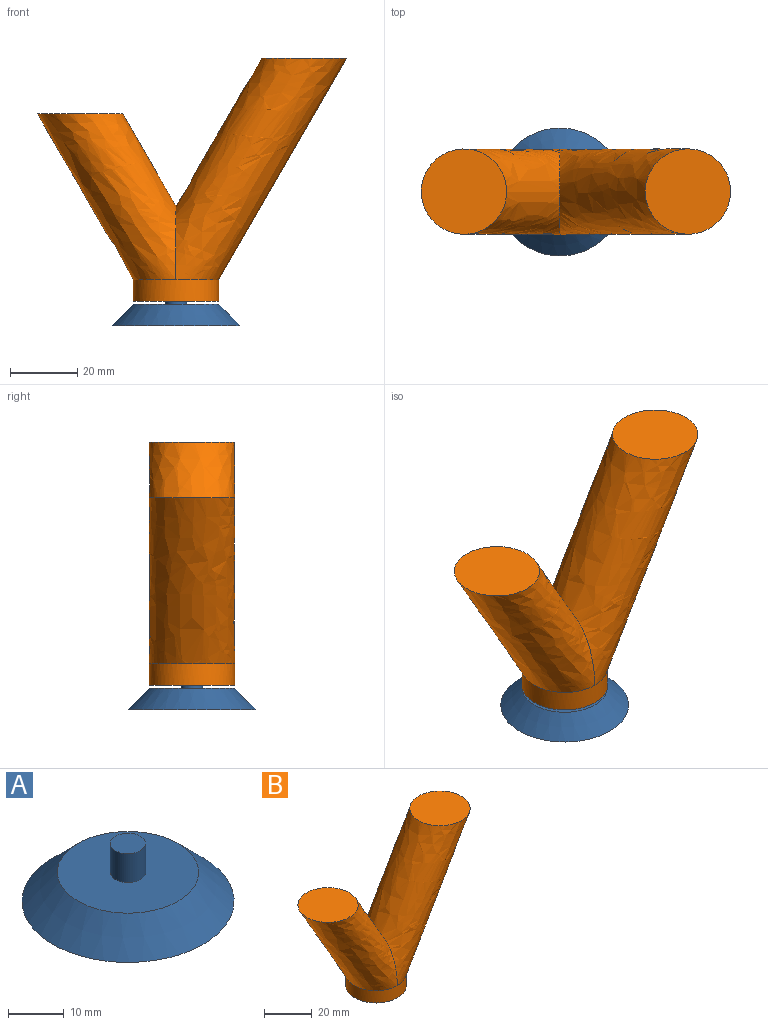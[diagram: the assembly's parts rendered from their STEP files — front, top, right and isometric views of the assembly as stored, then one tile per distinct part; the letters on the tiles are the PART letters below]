
ASSEMBLY  parts=2 mates=1
PART A: 5 faces, bbox 38.1x38.1x12.7 mm
  f0: plane 25.4x25.4mm, normal (0,0,1), area 475mm2, adj f2,f3
  f1: plane 38.1x38.1mm, normal (0,0,-1), area 1140.1mm2, adj f2
  f2: cone r=12.7mm half-angle=45deg, axis (0,0,-1), area 895.7mm2, adj f0,f1
  f3: cylinder r=3.17mm len=6.35mm, axis (0,0,-1), area 126.7mm2, adj f0,f4
  f4: plane 6.35x6.35mm, normal (0,0,1), area 31.7mm2, adj f3
PART B: 8 faces, bbox 95.6x54.3x75.9 mm
  f0: plane 28.93x28.93mm, normal (0,0,1), area 506.7mm2, adj f1
  f1: bspline ~65.99x63.5mm, area 5261.1mm2, adj f0,f3,f4
  f2: plane 28.93x28.93mm, normal (0,0,1), area 506.7mm2, adj f3
  f3: bspline ~53.98x50.8mm, area 3834.1mm2, adj f1,f2,f4
  f4: cylinder r=12.7mm len=25.4mm, axis (0,0,1), area 506.7mm2, adj f1,f3,f5
  f5: plane 25.4x25.4mm, normal (0,0,-1), area 475mm2, adj f4,f6
  f6: cylinder r=3.17mm len=6.35mm, axis (0,0,-1), area 126.7mm2, adj f5,f7
  f7: plane 6.35x6.35mm, normal (0,0,-1), area 31.7mm2, adj f6
PLACE A t=(4.1,-1.04,1.89)mm
PLACE B t=(4.1,-1.04,9.13)mm
MATE cylindrical A.f3 <-> B.f6  axis (0,0,-1) through (4.1,-1.04,5.06)mm
